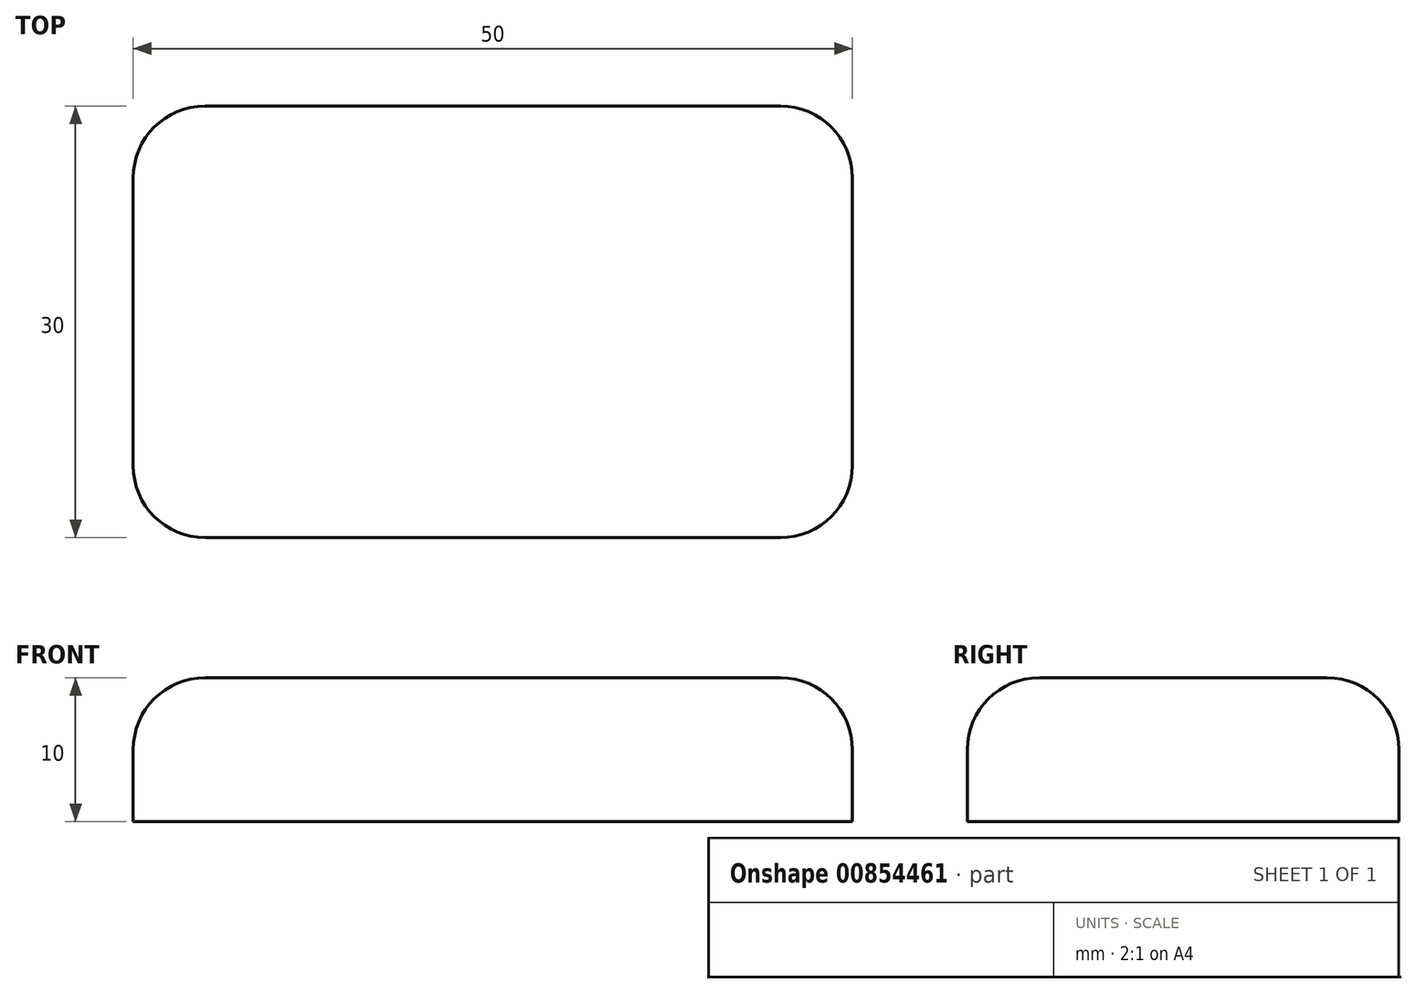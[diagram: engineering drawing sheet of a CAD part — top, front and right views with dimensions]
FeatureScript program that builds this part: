
annotation { "Feature Type Name" : "Feature", "Feature Type Description" : "" }
export const myFeature = defineFeature(function(context is Context, id is Id, definition is map)
    precondition{}
    {
        {
            var Q0;
            Q0=qCreatedBy(makeId("Top.planeOp"),FACE);
            var sketch = newSketch(context, id + "F0", { "sketchPlane" : qUnion([Q0])});
            skLineSegment(sketch, "E0.bottom", {"start": v(20, -15) * mm, "end": v(-20, -15) * mm});
            skLineSegment(sketch, "E0.top", {"start": v(20, 15) * mm, "end": v(-20, 15) * mm});
            skLineSegment(sketch, "E0.left", {"start": v(25, -10) * mm, "end": v(25, 10) * mm});
            skLineSegment(sketch, "E0.right", {"start": v(-25, -10) * mm, "end": v(-25, 10) * mm});
            skPoint(sketch, "E0.middle", {"position": v(0, 0) * mm});
            skPoint(sketch, "E1.visualSharp", {"position": v(-25, 15) * mm});
            skArc(sketch, "E1.filletArc", {"start": v(-20, 15) * mm, "mid": v(-23.54, 13.54) * mm, "end": v(-25, 10) * mm});
            skPoint(sketch, "E2.visualSharp", {"position": v(25, 15) * mm});
            skArc(sketch, "E2.filletArc", {"start": v(25, 10) * mm, "mid": v(23.54, 13.54) * mm, "end": v(20, 15) * mm});
            skPoint(sketch, "E3.visualSharp", {"position": v(25, -15) * mm});
            skArc(sketch, "E3.filletArc", {"start": v(20, -15) * mm, "mid": v(23.54, -13.54) * mm, "end": v(25, -10) * mm});
            skPoint(sketch, "E4.visualSharp", {"position": v(-25, -15) * mm});
            skArc(sketch, "E4.filletArc", {"start": v(-25, -10) * mm, "mid": v(-23.54, -13.54) * mm, "end": v(-20, -15) * mm});
            skSolve(sketch);
        }
        {
            var Q0;
            Q0=makeQuery(id+"F0.imprint","IMPRINT",FACE,{"disambiguationData":[TD([[makeQuery(id+"F0.imprint","IMPRINT",EDGE,{"derivedFrom":sQuery(id+"F0.wireOp",EDGE,"E0.bottom")}),-1.0]])]});
            extrude(context, id + "F1", {"entities" : qUnion([Q0]), "depth" : 10 * mm, "offsetDistance" : 25 * mm});
        }
        {
            var Q0;
            Q0=makeQuery(id+"F1.opExtrude","CAP_EDGE",EDGE,{"disambiguationData":[OSD([sQuery(id+"F0.wireOp",EDGE,"E0.right")])],"isStart":false});
            fillet(context, id + "F2", {"entities" : qUnion([Q0]), "radius" : 5 * mm, "tangentPropagation" : true, "allowEdgeOverflow" : false});
        }
    });
